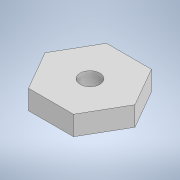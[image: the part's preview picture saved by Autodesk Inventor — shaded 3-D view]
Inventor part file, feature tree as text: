
AUTODESK INVENTOR PART (.ipt)
format: ipt  version: 2022 (Build 260153000, 153)  size: 97,792 bytes
history: native  units: mm
features: extrude x1, sketch x1
ambient origin geometry x8: Origin, YZ Plane, XZ Plane, XY Plane, X Axis, Y Axis, Z Axis, Center Point
bodies: Solid1 (feature_tree)
feature tree (2):
  extrude  "Extrusion1"  Depth=50.0mm TaperAngle=0.0deg
  sketch  "Sketch1"  dims[d0=100.0mm d1=50.0mm d2=0.0mm]
